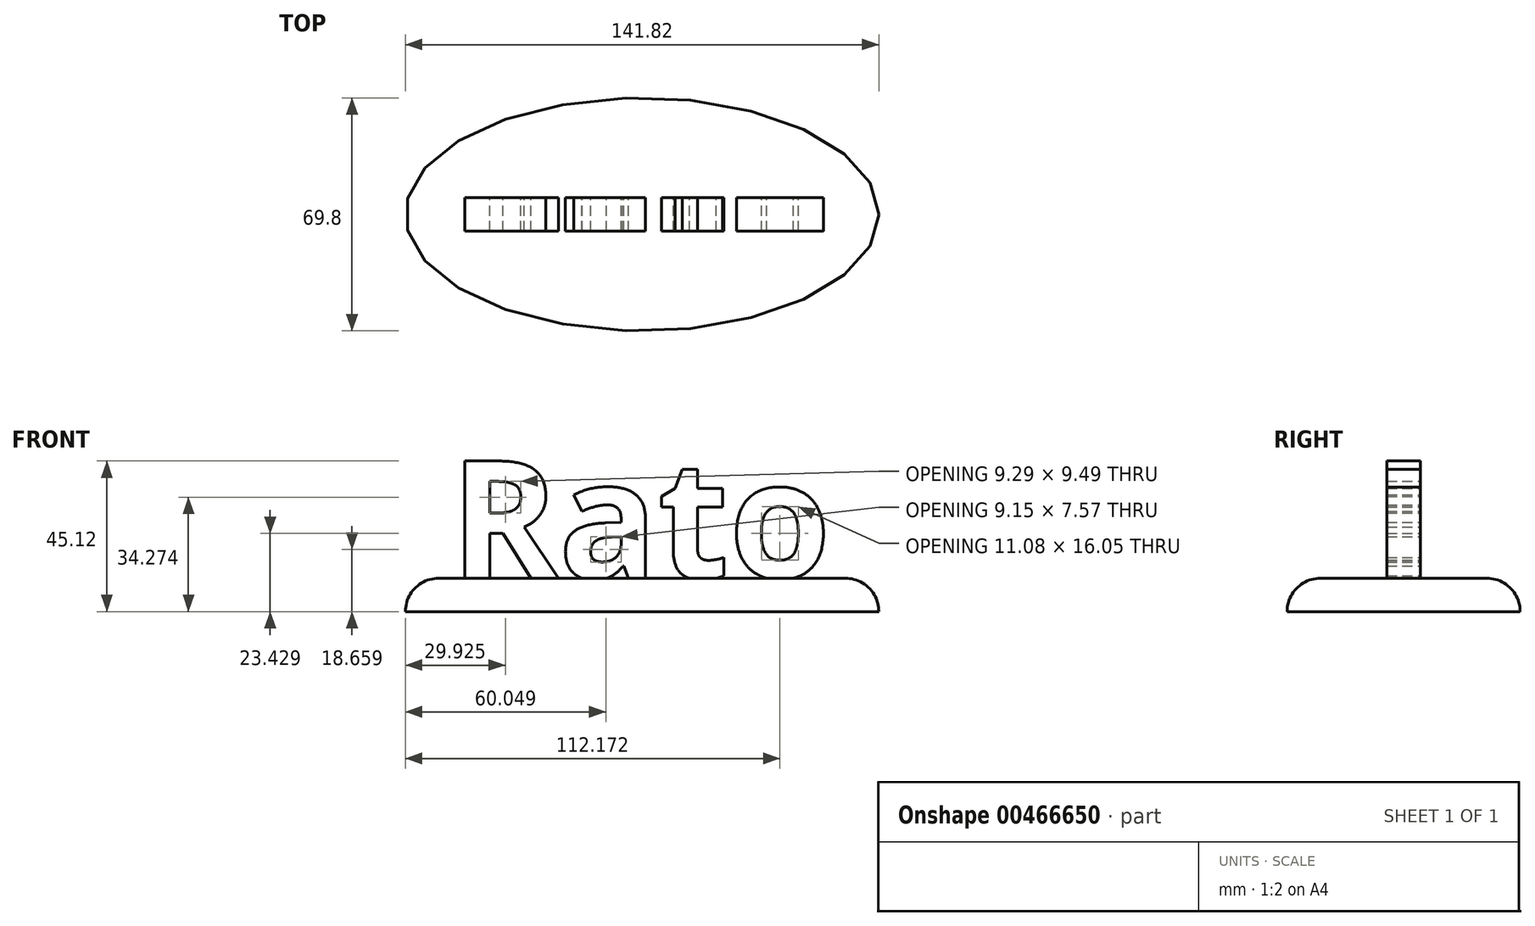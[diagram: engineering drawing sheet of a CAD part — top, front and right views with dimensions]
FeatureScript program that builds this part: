
annotation { "Feature Type Name" : "Feature", "Feature Type Description" : "" }
export const myFeature = defineFeature(function(context is Context, id is Id, definition is map)
    precondition{}
    {
        {
            var Q0;
            Q0=qCreatedBy(makeId("Top.planeOp"),FACE);
            var sketch = newSketch(context, id + "F0", { "sketchPlane" : qUnion([Q0])});
            skEllipse(sketch, "E0", {"center": v(0, 0) * mm, "majorRadius": 70.91 * mm, "minorRadius": 34.9 * mm, "majorAxis": v(1, 0)});
            skSolve(sketch);
        }
        {
            var Q0;
            Q0=qSketchRegion(id+"F0",true);
            extrude(context, id + "F1", {"entities" : qUnion([Q0]), "depth" : 10 * mm});
        }
        {
            var Q0;
            Q0=makeQuery(id+"F1.opExtrude","CAP_EDGE",EDGE,{"disambiguationData":[OSD([sQuery(id+"F0.wireOp",EDGE,"E0")])],"isStart":false});
            fillet(context, id + "F2", {"entities" : qUnion([Q0]), "radius" : 10 * mm, "tangentPropagation" : true, "allowEdgeOverflow" : false});
        }
        {
            var Q0;
            Q0=makeQuery(id+"F1.opExtrude","CAP_FACE",FACE,{"disambiguationData":[OSD([sQuery(id+"F0.wireOp",EDGE,"E0")])],"isStart":false});
            var sketch = newSketch(context, id + "F3", { "sketchPlane" : qUnion([Q0])});
            skLineSegment(sketch, "E1", {"start": v(-60.91, 0) * mm, "end": v(60.91, 0) * mm});
            skSolve(sketch);
        }
        {
            var Q0;
            Q0=qCreatedBy(makeId("Front.planeOp"),FACE);
            var sketch = newSketch(context, id + "F4", { "sketchPlane" : qUnion([Q0])});
            skText(sketch, "E2", { "text": "Rato", "fontName": "NotoSans-Bold.ttf"});
            const initialGuessF4  = {"E2": [-0.0575, 0.01, 1, 0, 0.03542]};
            skSetInitialGuess(sketch, initialGuessF4);
            skSolve(sketch);
        }
        {
            var Q0;
            Q0 = qSketchRegion(id + "F4", true);
            extrude(context, id + "F5", {"entities" : qUnion([Q0]), "operationType" : NewBodyOperationType.ADD, "depth" : 10 * mm, "symmetric" : true});
        }
    });
